# Revit family: Seating-LAMMHULTS-GRADE-Swivelbase
name_source: partatom
category: Furniture
revit_build: Autodesk Revit 2014 (Build: 20140709_2115(x64)
units: mm (PartAtom-declared; Revit-internal decimal feet)

## types (3) — shared parameters
Assembly Code = E2020
Depth = 780 mm
Description = *Please enter mtrl description here for use in mto*
Height = 540 mm
Keynote = 46.B
Manufacturer = LAMMHULTS
Model = GRADE
URL = www.lammhults.se
Weight = 8.0
Width = 530 mm

## per-type parameters (varying)
| type | Armrest Material | Frame Material | Seat Material | Seat Pad Material |
| Chrome - White | Metal - Chrome - Polished | Metal - Chrome - Polished | Colour - Coated - White | Fabric - Divina 3 - 236 |
| Coated - Pistachio | Colour - Coated - Pistachio | Colour - Coated - Pistachio | Colour - Coated - Pistachio | Fabric - Divina 3 - 384 |
| Coated - Fabric | Colour - Coated - Black | Colour - Coated - Black | Fabric - Divina 3 - 856 | Fabric - Divina 3 - 691 |

## geometry (parser evidence)
native form markers: Blend x442, Sweep x2
no freeform markers — native parametric forms only
